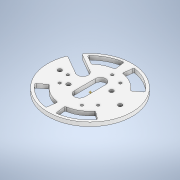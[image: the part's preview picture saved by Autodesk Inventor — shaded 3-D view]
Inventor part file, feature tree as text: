
AUTODESK INVENTOR PART (.ipt)
format: ipt  version: 2021 (Build 250183000, 183)  size: 187,392 bytes
history: mixed  units: in
note: dims shown in document units (in); Inventor stores cm internally (conversion verified against a paired STEP export)
features: move_body x1, fillet x1, imported_body x1
ambient origin geometry x8: Origin, YZ Plane, XZ Plane, XY Plane, X Axis, Y Axis, Z Axis, Center Point
bodies: Solid1 (imported_parasolid)
feature tree (3):
  move_body  "Move Body1"
  fillet  "Fillet3"  Radius=0.0415in
  imported_body  NMx_Import_Brep_tag  [imported B-rep: ~54 faces, bbox_mm=[169.039301, 9.525, 188.282505]]
